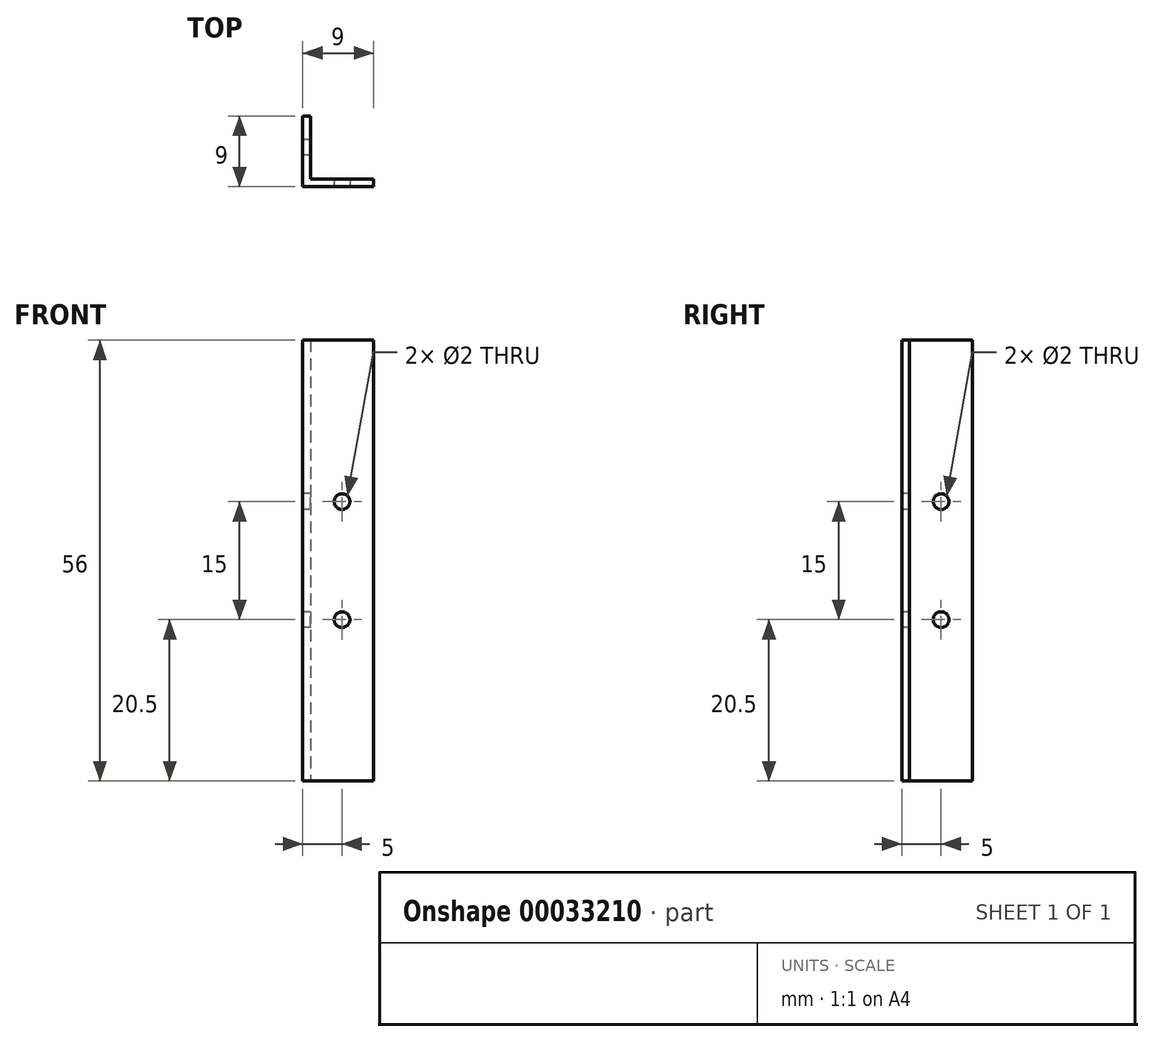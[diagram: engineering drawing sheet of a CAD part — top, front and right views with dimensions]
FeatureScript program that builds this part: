
annotation { "Feature Type Name" : "Feature", "Feature Type Description" : "" }
export const myFeature = defineFeature(function(context is Context, id is Id, definition is map)
    precondition{}
    {
        {
            var Q0;
            Q0=qCreatedBy(makeId("Top.planeOp"),FACE);
            var sketch = newSketch(context, id + "F0", { "sketchPlane" : qUnion([Q0])});
            skLineSegment(sketch, "E0.bottom", {"start": v(0, 0) * mm, "end": v(9, 0) * mm});
            skLineSegment(sketch, "E0.top", {"start": v(0, 9) * mm, "end": v(1, 9) * mm});
            skLineSegment(sketch, "E0.left", {"start": v(0, 0) * mm, "end": v(0, 9) * mm});
            skLineSegment(sketch, "E0.right", {"start": v(9, 0) * mm, "end": v(9, 1) * mm});
            skLineSegment(sketch, "E1.top", {"start": v(9, 1) * mm, "end": v(1, 1) * mm});
            skLineSegment(sketch, "E1.right", {"start": v(1, 9) * mm, "end": v(1, 1) * mm});
            skSolve(sketch);
        }
        {
            var Q0;
            Q0=qSketchRegion(id+"F0",true);
            extrude(context, id + "F1", {"entities" : qUnion([Q0]), "depth" : 56 * mm});
        }
        {
            var Q0;
            Q0=makeQuery(id+"F1.opExtrude","SWEPT_FACE",FACE,{"disambiguationData":[OSD([sQuery(id+"F0.wireOp",EDGE,"E0.bottom")])]});
            var sketch = newSketch(context, id + "F2", { "sketchPlane" : qUnion([Q0])});
            skLineSegment(sketch, "E2", {"start": v(0, 28) * mm, "end": v(9, 28) * mm, "construction": true});
            skCircle(sketch, "E3", {"center": v(5, 35.5) * mm, "radius": 1 * mm});
            skCircle(sketch, "E4.MirrorC", {"center": v(5, 20.5) * mm, "radius": 1 * mm});
            skSolve(sketch);
        }
        {
            var Q0;
            Q0=qSketchRegion(id+"F2",true);
            extrude(context, id + "F3", {"entities" : qUnion([Q0]), "operationType" : NewBodyOperationType.REMOVE, "endBound" : BoundingType.UP_TO_NEXT, "oppositeDirection" : true, "depth" : 25 * mm});
        }
        {
            var Q0;
            Q0=makeQuery(id+"F1.opExtrude","SWEPT_FACE",FACE,{"disambiguationData":[OSD([sQuery(id+"F0.wireOp",EDGE,"E0.left")])]});
            var sketch = newSketch(context, id + "F4", { "sketchPlane" : qUnion([Q0])});
            skLineSegment(sketch, "E5", {"start": v(-9, 28) * mm, "end": v(0, 28) * mm, "construction": true});
            skCircle(sketch, "E6", {"center": v(-5, 35.5) * mm, "radius": 1 * mm});
            skCircle(sketch, "E7.MirrorC", {"center": v(-5, 20.5) * mm, "radius": 1 * mm});
            skSolve(sketch);
        }
        {
            var Q0;
            Q0=qSketchRegion(id+"F4",true);
            extrude(context, id + "F5", {"entities" : qUnion([Q0]), "operationType" : NewBodyOperationType.REMOVE, "endBound" : BoundingType.UP_TO_NEXT, "oppositeDirection" : true, "depth" : 25 * mm});
        }
    });
